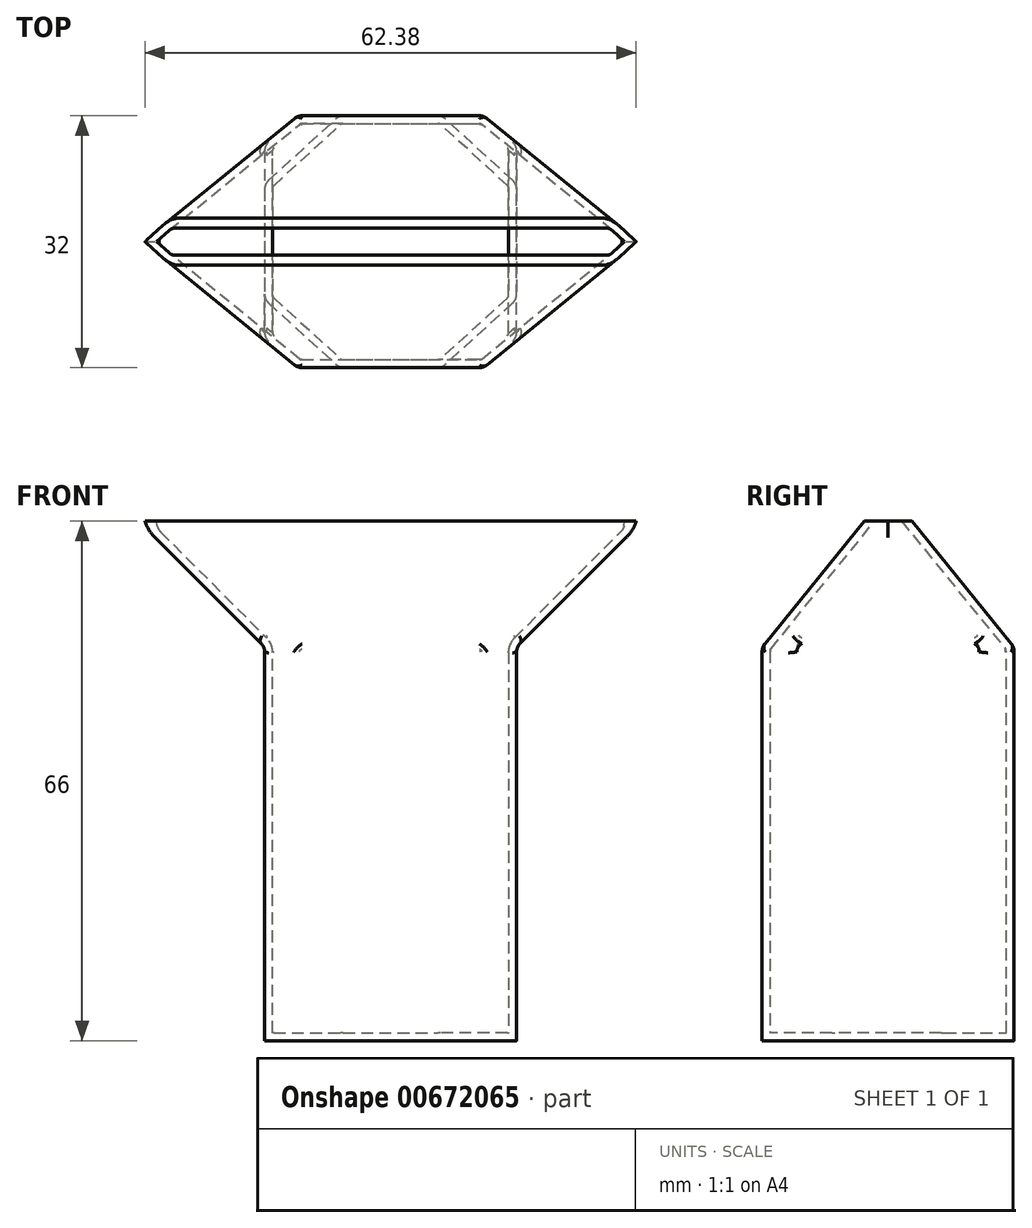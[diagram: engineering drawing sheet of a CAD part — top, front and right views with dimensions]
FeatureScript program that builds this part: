
annotation { "Feature Type Name" : "Feature", "Feature Type Description" : "" }
export const myFeature = defineFeature(function(context is Context, id is Id, definition is map)
    precondition{}
    {
        {
            assignVariable(context, id + "F0", {"name" : "length", "anyValue" : 32});
        }
        {
            assignVariable(context, id + "F1", {"name" : "depth", "anyValue" : 50});
        }
        {
            var Q0;
            Q0=qCreatedBy(makeId("Top.planeOp"),FACE);
            var sketch = newSketch(context, id + "F2", { "sketchPlane" : qUnion([Q0])});
            skLineSegment(sketch, "E0.bottom", {"start": v(-16, 16) * mm, "end": v(16, 16) * mm});
            skLineSegment(sketch, "E0.top", {"start": v(-16, -16) * mm, "end": v(16, -16) * mm});
            skLineSegment(sketch, "E0.left", {"start": v(-16, 16) * mm, "end": v(-16, -16) * mm});
            skLineSegment(sketch, "E0.right", {"start": v(16, 16) * mm, "end": v(16, -16) * mm});
            skPoint(sketch, "E0.middle", {"position": v(0, 0) * mm});
            skSolve(sketch);
        }
        {
            var Q0;
            Q0 = qSketchRegion(id + "F2", true);
            extrude(context, id + "F3", {"entities" : qUnion([Q0]), "depth" : (getVariable(context, 'depth')) * mm, "offsetDistance" : 25 * mm});
        }
        {
            var Q0;
            Q0=makeQuery(id+"F3.opExtrude","CAP_FACE",FACE,{"disambiguationData":[OSD([sQuery(id+"F2.wireOp",EDGE,"E0.bottom"),sQuery(id+"F2.wireOp",EDGE,"E0.top"),sQuery(id+"F2.wireOp",EDGE,"E0.left"),sQuery(id+"F2.wireOp",EDGE,"E0.right")])],"isStart":false});
            cPlane(context, id + "F4", {"entities" : qUnion([Q0]), "cplaneType" : CPlaneType.OFFSET, "offset" : (getVariable(context, 'length') / 2) * mm, "width" : 150 * mm, "height" : 150 * mm});
        }
        {
            var Q0;
            Q0=qCreatedBy(id+"F4.planeOp",FACE);
            var sketch = newSketch(context, id + "F5", { "sketchPlane" : qUnion([Q0])});
            skLineSegment(sketch, "E1.bottom", {"start": v(32, 3) * mm, "end": v(-32, 3) * mm});
            skLineSegment(sketch, "E1.top", {"start": v(32, -3) * mm, "end": v(-32, -3) * mm});
            skLineSegment(sketch, "E1.left", {"start": v(32, 3) * mm, "end": v(32, -3) * mm});
            skLineSegment(sketch, "E1.right", {"start": v(-32, 3) * mm, "end": v(-32, -3) * mm});
            skPoint(sketch, "E1.middle", {"position": v(0, 0) * mm});
            skSolve(sketch);
        }
        {
            var Q1;
            Q1=makeQuery(id+"F3.opExtrude","CAP_FACE",FACE,{"disambiguationData":[OSD([sQuery(id+"F2.wireOp",EDGE,"E0.bottom"),sQuery(id+"F2.wireOp",EDGE,"E0.top"),sQuery(id+"F2.wireOp",EDGE,"E0.left"),sQuery(id+"F2.wireOp",EDGE,"E0.right")])],"isStart":false});
            var Q2;
            Q2=makeQuery(id+"F5.imprint","IMPRINT",FACE,{"disambiguationData":[TD([[makeQuery(id+"F5.imprint","IMPRINT",EDGE,{"derivedFrom":sQuery(id+"F5.wireOp",EDGE,"E1.bottom")}),1.0]])]});
            loft(context, id + "F6", {"operationType" : NewBodyOperationType.ADD, "sheetProfilesArray" : [{ "sheetProfileEntities" : qUnion([Q1]) }, { "sheetProfileEntities" : qUnion([Q2]) }]});
        }
        {
            var Q0;
            Q0=makeQuery(id+"F6.opLoft","SWEPT_EDGE",EDGE,{"disambiguationData":[OSD([sQuery(id+"F2.wireOp",EDGE,"E0.top"),sQuery(id+"F2.wireOp",EDGE,"E0.left"),sQuery(id+"F5.wireOp",EDGE,"E1.top"),sQuery(id+"F5.wireOp",EDGE,"E1.right")])]});
            var Q1;
            Q1=makeQuery(id+"F6.opLoft","SWEPT_EDGE",EDGE,{"disambiguationData":[OSD([sQuery(id+"F2.wireOp",EDGE,"E0.bottom"),sQuery(id+"F2.wireOp",EDGE,"E0.left"),sQuery(id+"F5.wireOp",EDGE,"E1.bottom"),sQuery(id+"F5.wireOp",EDGE,"E1.right")])]});
            var Q2;
            Q2=makeQuery(id+"F6.opLoft","SWEPT_EDGE",EDGE,{"disambiguationData":[OSD([sQuery(id+"F2.wireOp",EDGE,"E0.top"),sQuery(id+"F2.wireOp",EDGE,"E0.right"),sQuery(id+"F5.wireOp",EDGE,"E1.top"),sQuery(id+"F5.wireOp",EDGE,"E1.left")])]});
            var Q3;
            Q3=makeQuery(id+"F6.opLoft","SWEPT_EDGE",EDGE,{"disambiguationData":[OSD([sQuery(id+"F2.wireOp",EDGE,"E0.bottom"),sQuery(id+"F2.wireOp",EDGE,"E0.right"),sQuery(id+"F5.wireOp",EDGE,"E1.bottom"),sQuery(id+"F5.wireOp",EDGE,"E1.left")])]});
            chamfer(context, id + "F7", {"entities" : qUnion([Q0, Q1, Q2, Q3]), "width" : 2 * mm, "tangentPropagation" : true});
        }
        {
            var Q0;
            {var subQ0=sQuery(id+"F2.wireOp",EDGE,"E0.top");Q0=makeQuery(id+"F7.opChamfer","BLEND_EDGE",EDGE,{"blendedFrom":[makeQuery(id+"F6.opLoft","SWEPT_EDGE",EDGE,{"disambiguationData":[OSD([subQ0,sQuery(id+"F2.wireOp",EDGE,"E0.left"),sQuery(id+"F5.wireOp",EDGE,"E1.top"),sQuery(id+"F5.wireOp",EDGE,"E1.right")])]}),makeQuery(id+"F3.opExtrude","SWEPT_FACE",FACE,{"disambiguationData":[OSD([subQ0])]})],"blendedInto":[makeQuery(id+"F3.opExtrude","SWEPT_FACE",FACE,{"disambiguationData":[OSD([subQ0])]})]});}
            var Q1;
            {var subQ0=sQuery(id+"F2.wireOp",EDGE,"E0.left");Q1=makeQuery(id+"F7.opChamfer","BLEND_EDGE",EDGE,{"blendedFrom":[makeQuery(id+"F6.opLoft","SWEPT_EDGE",EDGE,{"disambiguationData":[OSD([sQuery(id+"F2.wireOp",EDGE,"E0.top"),subQ0,sQuery(id+"F5.wireOp",EDGE,"E1.top"),sQuery(id+"F5.wireOp",EDGE,"E1.right")])]}),makeQuery(id+"F3.opExtrude","SWEPT_FACE",FACE,{"disambiguationData":[OSD([subQ0])]})],"blendedInto":[makeQuery(id+"F3.opExtrude","SWEPT_FACE",FACE,{"disambiguationData":[OSD([subQ0])]})]});}
            var Q2;
            {var subQ0=sQuery(id+"F5.wireOp",EDGE,"E1.right");var subQ1=sQuery(id+"F5.wireOp",EDGE,"E1.top");var subQ2=sQuery(id+"F2.wireOp",EDGE,"E0.left");var subQ3=sQuery(id+"F2.wireOp",EDGE,"E0.top");Q2=makeQuery(id+"F7.opChamfer","BLEND_EDGE",EDGE,{"blendedFrom":[makeQuery(id+"F6.opLoft","SWEPT_EDGE",EDGE,{"disambiguationData":[OSD([subQ3,subQ2,subQ1,subQ0])]}),makeQuery(id+"F6.opLoft","SWEPT_FACE",FACE,{"disambiguationData":[OSD([sQuery(id+"F2.wireOp",EDGE,"E0.bottom"),subQ3,subQ2,sQuery(id+"F5.wireOp",EDGE,"E1.bottom"),subQ1,subQ0])]})],"blendedInto":[makeQuery(id+"F6.opLoft","SWEPT_FACE",FACE,{"disambiguationData":[OSD([sQuery(id+"F2.wireOp",EDGE,"E0.bottom"),subQ3,subQ2,sQuery(id+"F5.wireOp",EDGE,"E1.bottom"),subQ1,subQ0])]})]});}
            var Q3;
            {var subQ0=sQuery(id+"F5.wireOp",EDGE,"E1.right");var subQ1=sQuery(id+"F5.wireOp",EDGE,"E1.top");var subQ2=sQuery(id+"F2.wireOp",EDGE,"E0.left");var subQ3=sQuery(id+"F2.wireOp",EDGE,"E0.top");Q3=makeQuery(id+"F7.opChamfer","BLEND_EDGE",EDGE,{"blendedFrom":[makeQuery(id+"F6.opLoft","SWEPT_EDGE",EDGE,{"disambiguationData":[OSD([subQ3,subQ2,subQ1,subQ0])]}),makeQuery(id+"F6.opLoft","SWEPT_FACE",FACE,{"disambiguationData":[OSD([subQ3,subQ2,sQuery(id+"F2.wireOp",EDGE,"E0.right"),subQ1,sQuery(id+"F5.wireOp",EDGE,"E1.left"),subQ0])]})],"blendedInto":[makeQuery(id+"F6.opLoft","SWEPT_FACE",FACE,{"disambiguationData":[OSD([subQ3,subQ2,sQuery(id+"F2.wireOp",EDGE,"E0.right"),subQ1,sQuery(id+"F5.wireOp",EDGE,"E1.left"),subQ0])]})]});}
            var Q4;
            {var subQ0=sQuery(id+"F5.wireOp",EDGE,"E1.right");var subQ1=sQuery(id+"F5.wireOp",EDGE,"E1.bottom");var subQ2=sQuery(id+"F2.wireOp",EDGE,"E0.left");var subQ3=sQuery(id+"F2.wireOp",EDGE,"E0.bottom");Q4=makeQuery(id+"F7.opChamfer","BLEND_EDGE",EDGE,{"blendedFrom":[makeQuery(id+"F6.opLoft","SWEPT_EDGE",EDGE,{"disambiguationData":[OSD([subQ3,subQ2,subQ1,subQ0])]}),makeQuery(id+"F6.opLoft","SWEPT_FACE",FACE,{"disambiguationData":[OSD([subQ3,sQuery(id+"F2.wireOp",EDGE,"E0.top"),subQ2,subQ1,sQuery(id+"F5.wireOp",EDGE,"E1.top"),subQ0])]})],"blendedInto":[makeQuery(id+"F6.opLoft","SWEPT_FACE",FACE,{"disambiguationData":[OSD([subQ3,sQuery(id+"F2.wireOp",EDGE,"E0.top"),subQ2,subQ1,sQuery(id+"F5.wireOp",EDGE,"E1.top"),subQ0])]})]});}
            var Q5;
            {var subQ0=sQuery(id+"F2.wireOp",EDGE,"E0.left");Q5=makeQuery(id+"F7.opChamfer","BLEND_EDGE",EDGE,{"blendedFrom":[makeQuery(id+"F6.opLoft","SWEPT_EDGE",EDGE,{"disambiguationData":[OSD([sQuery(id+"F2.wireOp",EDGE,"E0.bottom"),subQ0,sQuery(id+"F5.wireOp",EDGE,"E1.bottom"),sQuery(id+"F5.wireOp",EDGE,"E1.right")])]}),makeQuery(id+"F3.opExtrude","SWEPT_FACE",FACE,{"disambiguationData":[OSD([subQ0])]})],"blendedInto":[makeQuery(id+"F3.opExtrude","SWEPT_FACE",FACE,{"disambiguationData":[OSD([subQ0])]})]});}
            var Q6;
            {var subQ0=sQuery(id+"F2.wireOp",EDGE,"E0.bottom");Q6=makeQuery(id+"F7.opChamfer","BLEND_EDGE",EDGE,{"blendedFrom":[makeQuery(id+"F6.opLoft","SWEPT_EDGE",EDGE,{"disambiguationData":[OSD([subQ0,sQuery(id+"F2.wireOp",EDGE,"E0.left"),sQuery(id+"F5.wireOp",EDGE,"E1.bottom"),sQuery(id+"F5.wireOp",EDGE,"E1.right")])]}),makeQuery(id+"F3.opExtrude","SWEPT_FACE",FACE,{"disambiguationData":[OSD([subQ0])]})],"blendedInto":[makeQuery(id+"F3.opExtrude","SWEPT_FACE",FACE,{"disambiguationData":[OSD([subQ0])]})]});}
            var Q7;
            {var subQ0=sQuery(id+"F5.wireOp",EDGE,"E1.right");var subQ1=sQuery(id+"F5.wireOp",EDGE,"E1.bottom");var subQ2=sQuery(id+"F2.wireOp",EDGE,"E0.left");var subQ3=sQuery(id+"F2.wireOp",EDGE,"E0.bottom");Q7=makeQuery(id+"F7.opChamfer","BLEND_EDGE",EDGE,{"blendedFrom":[makeQuery(id+"F6.opLoft","SWEPT_EDGE",EDGE,{"disambiguationData":[OSD([subQ3,subQ2,subQ1,subQ0])]}),makeQuery(id+"F6.opLoft","SWEPT_FACE",FACE,{"disambiguationData":[OSD([subQ3,subQ2,sQuery(id+"F2.wireOp",EDGE,"E0.right"),subQ1,sQuery(id+"F5.wireOp",EDGE,"E1.left"),subQ0])]})],"blendedInto":[makeQuery(id+"F6.opLoft","SWEPT_FACE",FACE,{"disambiguationData":[OSD([subQ3,subQ2,sQuery(id+"F2.wireOp",EDGE,"E0.right"),subQ1,sQuery(id+"F5.wireOp",EDGE,"E1.left"),subQ0])]})]});}
            var Q8;
            {var subQ0=sQuery(id+"F2.wireOp",EDGE,"E0.bottom");Q8=makeQuery(id+"F7.opChamfer","BLEND_EDGE",EDGE,{"blendedFrom":[makeQuery(id+"F6.opLoft","SWEPT_EDGE",EDGE,{"disambiguationData":[OSD([subQ0,sQuery(id+"F2.wireOp",EDGE,"E0.right"),sQuery(id+"F5.wireOp",EDGE,"E1.bottom"),sQuery(id+"F5.wireOp",EDGE,"E1.left")])]}),makeQuery(id+"F3.opExtrude","SWEPT_FACE",FACE,{"disambiguationData":[OSD([subQ0])]})],"blendedInto":[makeQuery(id+"F3.opExtrude","SWEPT_FACE",FACE,{"disambiguationData":[OSD([subQ0])]})]});}
            var Q9;
            {var subQ0=sQuery(id+"F5.wireOp",EDGE,"E1.left");var subQ1=sQuery(id+"F5.wireOp",EDGE,"E1.bottom");var subQ2=sQuery(id+"F2.wireOp",EDGE,"E0.right");var subQ3=sQuery(id+"F2.wireOp",EDGE,"E0.bottom");Q9=makeQuery(id+"F7.opChamfer","BLEND_EDGE",EDGE,{"blendedFrom":[makeQuery(id+"F6.opLoft","SWEPT_EDGE",EDGE,{"disambiguationData":[OSD([subQ3,subQ2,subQ1,subQ0])]}),makeQuery(id+"F6.opLoft","SWEPT_FACE",FACE,{"disambiguationData":[OSD([subQ3,sQuery(id+"F2.wireOp",EDGE,"E0.left"),subQ2,subQ1,subQ0,sQuery(id+"F5.wireOp",EDGE,"E1.right")])]})],"blendedInto":[makeQuery(id+"F6.opLoft","SWEPT_FACE",FACE,{"disambiguationData":[OSD([subQ3,sQuery(id+"F2.wireOp",EDGE,"E0.left"),subQ2,subQ1,subQ0,sQuery(id+"F5.wireOp",EDGE,"E1.right")])]})]});}
            var Q10;
            {var subQ0=sQuery(id+"F5.wireOp",EDGE,"E1.left");var subQ1=sQuery(id+"F5.wireOp",EDGE,"E1.bottom");var subQ2=sQuery(id+"F2.wireOp",EDGE,"E0.right");var subQ3=sQuery(id+"F2.wireOp",EDGE,"E0.bottom");Q10=makeQuery(id+"F7.opChamfer","BLEND_EDGE",EDGE,{"blendedFrom":[makeQuery(id+"F6.opLoft","SWEPT_EDGE",EDGE,{"disambiguationData":[OSD([subQ3,subQ2,subQ1,subQ0])]}),makeQuery(id+"F6.opLoft","SWEPT_FACE",FACE,{"disambiguationData":[OSD([subQ3,sQuery(id+"F2.wireOp",EDGE,"E0.top"),subQ2,subQ1,sQuery(id+"F5.wireOp",EDGE,"E1.top"),subQ0])]})],"blendedInto":[makeQuery(id+"F6.opLoft","SWEPT_FACE",FACE,{"disambiguationData":[OSD([subQ3,sQuery(id+"F2.wireOp",EDGE,"E0.top"),subQ2,subQ1,sQuery(id+"F5.wireOp",EDGE,"E1.top"),subQ0])]})]});}
            var Q11;
            {var subQ0=sQuery(id+"F2.wireOp",EDGE,"E0.right");Q11=makeQuery(id+"F7.opChamfer","BLEND_EDGE",EDGE,{"blendedFrom":[makeQuery(id+"F6.opLoft","SWEPT_EDGE",EDGE,{"disambiguationData":[OSD([sQuery(id+"F2.wireOp",EDGE,"E0.bottom"),subQ0,sQuery(id+"F5.wireOp",EDGE,"E1.bottom"),sQuery(id+"F5.wireOp",EDGE,"E1.left")])]}),makeQuery(id+"F3.opExtrude","SWEPT_FACE",FACE,{"disambiguationData":[OSD([subQ0])]})],"blendedInto":[makeQuery(id+"F3.opExtrude","SWEPT_FACE",FACE,{"disambiguationData":[OSD([subQ0])]})]});}
            var Q12;
            {var subQ0=sQuery(id+"F2.wireOp",EDGE,"E0.right");Q12=makeQuery(id+"F7.opChamfer","BLEND_EDGE",EDGE,{"blendedFrom":[makeQuery(id+"F6.opLoft","SWEPT_EDGE",EDGE,{"disambiguationData":[OSD([sQuery(id+"F2.wireOp",EDGE,"E0.top"),subQ0,sQuery(id+"F5.wireOp",EDGE,"E1.top"),sQuery(id+"F5.wireOp",EDGE,"E1.left")])]}),makeQuery(id+"F3.opExtrude","SWEPT_FACE",FACE,{"disambiguationData":[OSD([subQ0])]})],"blendedInto":[makeQuery(id+"F3.opExtrude","SWEPT_FACE",FACE,{"disambiguationData":[OSD([subQ0])]})]});}
            var Q13;
            {var subQ0=sQuery(id+"F5.wireOp",EDGE,"E1.left");var subQ1=sQuery(id+"F5.wireOp",EDGE,"E1.top");var subQ2=sQuery(id+"F2.wireOp",EDGE,"E0.right");var subQ3=sQuery(id+"F2.wireOp",EDGE,"E0.top");Q13=makeQuery(id+"F7.opChamfer","BLEND_EDGE",EDGE,{"blendedFrom":[makeQuery(id+"F6.opLoft","SWEPT_EDGE",EDGE,{"disambiguationData":[OSD([subQ3,subQ2,subQ1,subQ0])]}),makeQuery(id+"F6.opLoft","SWEPT_FACE",FACE,{"disambiguationData":[OSD([sQuery(id+"F2.wireOp",EDGE,"E0.bottom"),subQ3,subQ2,sQuery(id+"F5.wireOp",EDGE,"E1.bottom"),subQ1,subQ0])]})],"blendedInto":[makeQuery(id+"F6.opLoft","SWEPT_FACE",FACE,{"disambiguationData":[OSD([sQuery(id+"F2.wireOp",EDGE,"E0.bottom"),subQ3,subQ2,sQuery(id+"F5.wireOp",EDGE,"E1.bottom"),subQ1,subQ0])]})]});}
            var Q14;
            {var subQ0=sQuery(id+"F5.wireOp",EDGE,"E1.left");var subQ1=sQuery(id+"F5.wireOp",EDGE,"E1.top");var subQ2=sQuery(id+"F2.wireOp",EDGE,"E0.right");var subQ3=sQuery(id+"F2.wireOp",EDGE,"E0.top");Q14=makeQuery(id+"F7.opChamfer","BLEND_EDGE",EDGE,{"blendedFrom":[makeQuery(id+"F6.opLoft","SWEPT_EDGE",EDGE,{"disambiguationData":[OSD([subQ3,subQ2,subQ1,subQ0])]}),makeQuery(id+"F6.opLoft","SWEPT_FACE",FACE,{"disambiguationData":[OSD([subQ3,sQuery(id+"F2.wireOp",EDGE,"E0.left"),subQ2,subQ1,subQ0,sQuery(id+"F5.wireOp",EDGE,"E1.right")])]})],"blendedInto":[makeQuery(id+"F6.opLoft","SWEPT_FACE",FACE,{"disambiguationData":[OSD([subQ3,sQuery(id+"F2.wireOp",EDGE,"E0.left"),subQ2,subQ1,subQ0,sQuery(id+"F5.wireOp",EDGE,"E1.right")])]})]});}
            var Q15;
            {var subQ0=sQuery(id+"F2.wireOp",EDGE,"E0.top");Q15=makeQuery(id+"F7.opChamfer","BLEND_EDGE",EDGE,{"blendedFrom":[makeQuery(id+"F6.opLoft","SWEPT_EDGE",EDGE,{"disambiguationData":[OSD([subQ0,sQuery(id+"F2.wireOp",EDGE,"E0.right"),sQuery(id+"F5.wireOp",EDGE,"E1.top"),sQuery(id+"F5.wireOp",EDGE,"E1.left")])]}),makeQuery(id+"F3.opExtrude","SWEPT_FACE",FACE,{"disambiguationData":[OSD([subQ0])]})],"blendedInto":[makeQuery(id+"F3.opExtrude","SWEPT_FACE",FACE,{"disambiguationData":[OSD([subQ0])]})]});}
            var Q16;
            {var subQ0=sQuery(id+"F2.wireOp",EDGE,"E0.right");Q16=makeQuery(id+"F6.boolean.opBoolean","MERGE",EDGE,{"derivedFrom":[makeQuery(id+"F3.opExtrude","CAP_EDGE",EDGE,{"disambiguationData":[OSD([subQ0])],"isStart":false}),makeQuery(id+"F6.opLoft","MID_CAP_EDGE",EDGE,{"disambiguationData":[OSD([sQuery(id+"F2.wireOp",EDGE,"E0.bottom"),sQuery(id+"F2.wireOp",EDGE,"E0.top"),subQ0])],"capPos":0.0})]});}
            var Q17;
            {var subQ0=sQuery(id+"F2.wireOp",EDGE,"E0.left");Q17=makeQuery(id+"F6.boolean.opBoolean","MERGE",EDGE,{"derivedFrom":[makeQuery(id+"F3.opExtrude","CAP_EDGE",EDGE,{"disambiguationData":[OSD([subQ0])],"isStart":false}),makeQuery(id+"F6.opLoft","MID_CAP_EDGE",EDGE,{"disambiguationData":[OSD([sQuery(id+"F2.wireOp",EDGE,"E0.bottom"),sQuery(id+"F2.wireOp",EDGE,"E0.top"),subQ0])],"capPos":0.0})]});}
            var Q18;
            {var subQ0=sQuery(id+"F2.wireOp",EDGE,"E0.top");Q18=makeQuery(id+"F6.boolean.opBoolean","MERGE",EDGE,{"derivedFrom":[makeQuery(id+"F3.opExtrude","CAP_EDGE",EDGE,{"disambiguationData":[OSD([subQ0])],"isStart":false}),makeQuery(id+"F6.opLoft","MID_CAP_EDGE",EDGE,{"disambiguationData":[OSD([subQ0,sQuery(id+"F2.wireOp",EDGE,"E0.left"),sQuery(id+"F2.wireOp",EDGE,"E0.right")])],"capPos":0.0})]});}
            var Q19;
            {var subQ0=sQuery(id+"F2.wireOp",EDGE,"E0.bottom");Q19=makeQuery(id+"F6.boolean.opBoolean","MERGE",EDGE,{"derivedFrom":[makeQuery(id+"F3.opExtrude","CAP_EDGE",EDGE,{"disambiguationData":[OSD([subQ0])],"isStart":false}),makeQuery(id+"F6.opLoft","MID_CAP_EDGE",EDGE,{"disambiguationData":[OSD([subQ0,sQuery(id+"F2.wireOp",EDGE,"E0.left"),sQuery(id+"F2.wireOp",EDGE,"E0.right")])],"capPos":0.0})]});}
            fillet(context, id + "F8", {"entities" : qUnion([Q0, Q1, Q2, Q3, Q4, Q5, Q6, Q7, Q8, Q9, Q10, Q11, Q12, Q13, Q14, Q15, Q16, Q17, Q18, Q19]), "radius" : 1.5 * mm, "tangentPropagation" : true, "allowEdgeOverflow" : false});
        }
        {
            var Q0;
            Q0=makeQuery(id+"F6.opLoft","CAP_FACE",FACE,{"disambiguationData":[OSD([makeQuery(id+"F5.imprint","IMPRINT",FACE,{"disambiguationData":[TD([[makeQuery(id+"F5.imprint","IMPRINT",EDGE,{"derivedFrom":sQuery(id+"F5.wireOp",EDGE,"E1.bottom")}),1.0]])]})])],"isStart":true});
            shell(context, id + "F9", {"entities" : qUnion([Q0]), "thickness" : 1 * mm});
        }
    });
